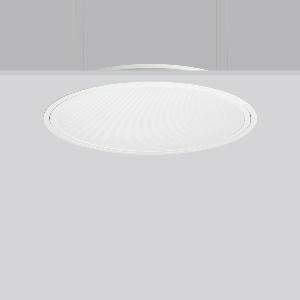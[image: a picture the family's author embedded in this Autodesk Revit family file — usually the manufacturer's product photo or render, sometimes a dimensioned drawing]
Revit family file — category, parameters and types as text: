
# Revit family: triona_round_e_312296_002_1_12_2006
name_source: partatom
category: Lighting Fixtures
units: mm (PartAtom-declared; Revit-internal decimal feet)

## family parameters
Cut with Voids When Loaded = No
Host = Face
Light Source = No
Part Type = Normal
Room Calculation Point = No
Round Connector Dimension = Use Diameter
Shared = No

## types (1)
- TRIONA round E (1 x LED Modul 840, 3900 lm, 4000)
    Apparent Load = 31 VA
    CIE Flux Codes = 58 86 97 100 100
    Color Rendering = 80
    Color Temperature = 4000
    Default Elevation = 1800 mm
    Description = Series: TRIONA round
Decorative round LED recessed surface luminaire. Cover made of sheet steel, powder-coated. Frame made of aluminium, powder-coated. Recessed ring: aluminium extrusion profile, powder coated. Light emission through a diffuser in plastic, opal/prismatic. Lightguide and diffuser made of non-yellowing plastic (PMMA). Lateral light emission (RZB SIDELITE technology) for above-average homogeneous light distribution. Suitable for installation in cavity ceilings. Tool-free mounting system thanks to the rocker arm mechanism (patent pending). Electronic ballast included. Very easy installation thanks to Plug+Play connection. Perfect for office areas (RUG < 19) and environments with computer screens in accordance with EN 12464-1. 
Colour: traffic white, matt (RAL 9016)
Diameter: 725 mm
Height: 2 mm
Cut-out diameter: 702 mm
Recess height: 100 mm
Luminaire: recess height: 89 mm
Lamp: LED
Socket: without socket
Colour temperature: 4000K
Colour rendering index (CRI): 80
System power: 31 W
Rated luminous flux: 3900 lm
Luminous efficiency: 126 lm/W
Control gear: Converter, dimmable, DALI
Protection class: I
Type of protection: IP 40
    Height = 0 mm  [stored 0 ft]
    Lamp = 1 x LED Modul 840
    Lamp Light Flux = 3900 lm
    Lamp count = 1
    Length = 725 mm
    Lifetime = 50000 h
    Luminous efficacy = 126 lm/W
    Manufacturer = RZB
    ModVariant = No
    Model = 312296.002.1.12
    Mounting Place = Ceiling
    Mounting Type = Recessed
    Number of Poles = 1
    OnlyDefault = Yes
    Power Factor = 1
    Product Name = TRIONA round E
    Product group = Recessed modular luminaires
    ProductGroupID = 406
    Protection Class = Protection class I
    Protection Degree = IP 20
    RLX_Detail_Level = 1
    RLX_Emergency_Light_Flux = 0 lm
    RLX_Emergency_Type = 0
    RLX_Emergency_Type_DB = No
    RlxData = <blob elided: 35505 chars, md5=6c203128>
    Socket = socket
    Standby Power = 0 W
    System Light Flux = 3900 lm
    System Power = 31 W
    Type Comments = Product without accessories
    Type Image = 312296.002.12.jpg
    URL = http://relux.com
    VarID = ---
    Voltage = 230 V
    Voltage Range = 220-240 V
    Weight = 0.00 kg
    Width = 0 mm  [stored 0 ft]

note: [stored X ft] marks values corroborated as IEEE doubles in the binary element streams (Revit-internal decimal feet)

## geometry (parser evidence)
native form markers: Blend x4, Sweep x10
no freeform markers — native parametric forms only
